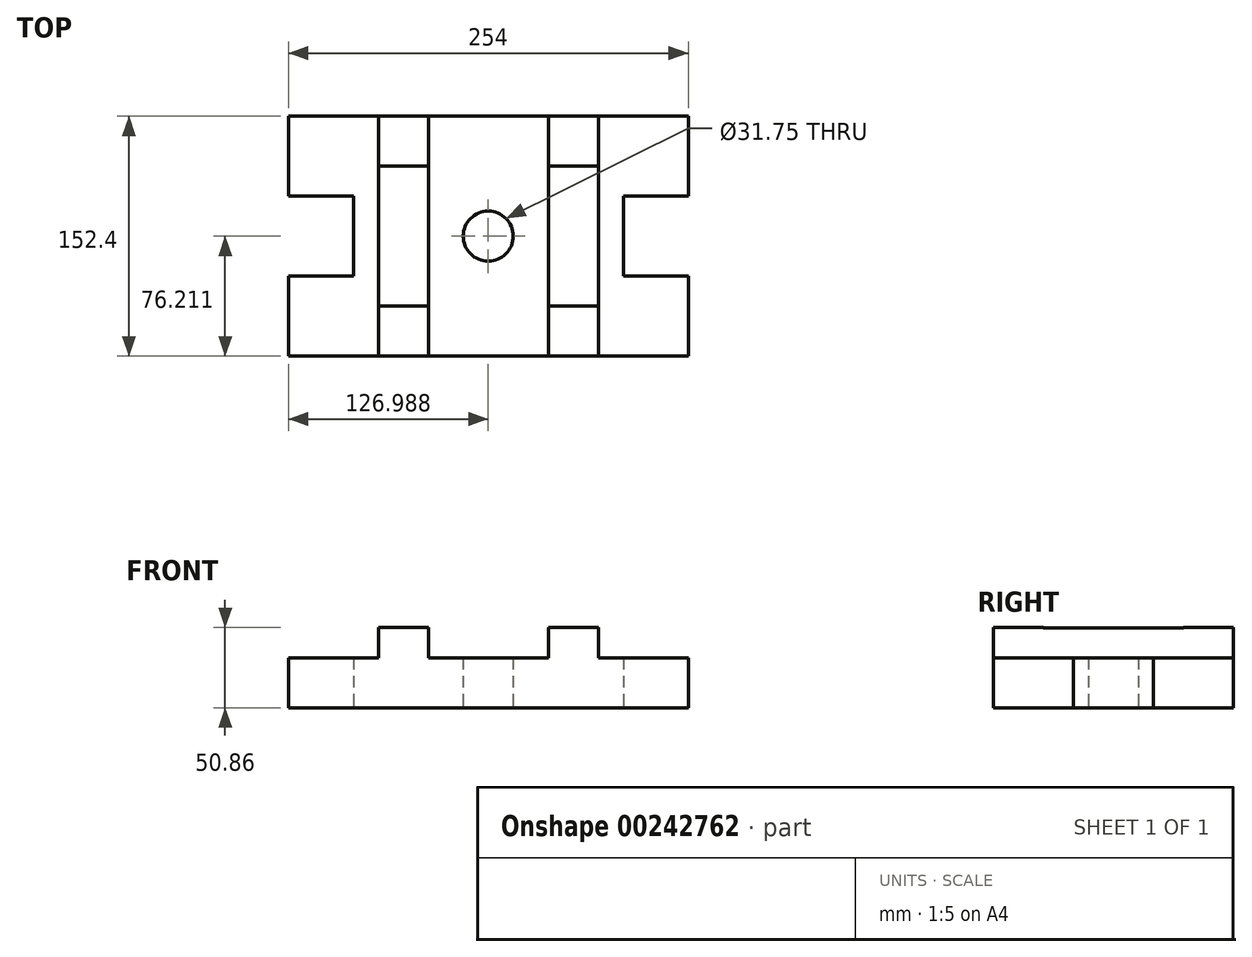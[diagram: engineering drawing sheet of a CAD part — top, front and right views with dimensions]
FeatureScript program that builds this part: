
annotation { "Feature Type Name" : "Feature", "Feature Type Description" : "" }
export const myFeature = defineFeature(function(context is Context, id is Id, definition is map)
    precondition{}
    {
        {
            var Q0;
            Q0=qCreatedBy(makeId("Top.planeOp"),FACE);
            var sketch = newSketch(context, id + "F0", { "sketchPlane" : qUnion([Q0])});
            skLineSegment(sketch, "E0.bottom", {"start": v(-75.13, 76.78) * mm, "end": v(96.32, 76.78) * mm});
            skLineSegment(sketch, "E0.top", {"start": v(-75.13, -75.62) * mm, "end": v(96.32, -75.62) * mm});
            skLineSegment(sketch, "E0.left", {"start": v(-75.13, 76.78) * mm, "end": v(-75.13, -75.62) * mm});
            skLineSegment(sketch, "E0.right", {"start": v(96.32, 76.78) * mm, "end": v(96.32, -75.62) * mm});
            skLineSegment(sketch, "E1.bottom", {"start": v(96.32, 76.78) * mm, "end": v(137.6, 76.78) * mm});
            skLineSegment(sketch, "E1.top", {"start": v(96.32, 25.98) * mm, "end": v(137.6, 25.98) * mm});
            skLineSegment(sketch, "E1.left", {"start": v(96.32, 76.78) * mm, "end": v(96.32, 25.98) * mm});
            skLineSegment(sketch, "E1.right", {"start": v(137.6, 76.78) * mm, "end": v(137.6, 25.98) * mm});
            skLineSegment(sketch, "E2.bottom", {"start": v(96.32, -75.62) * mm, "end": v(137.6, -75.62) * mm});
            skLineSegment(sketch, "E2.top", {"start": v(96.32, -24.82) * mm, "end": v(137.6, -24.82) * mm});
            skLineSegment(sketch, "E2.left", {"start": v(96.32, -75.62) * mm, "end": v(96.32, -24.82) * mm});
            skLineSegment(sketch, "E2.right", {"start": v(137.6, -75.62) * mm, "end": v(137.6, -24.82) * mm});
            skLineSegment(sketch, "E3.bottom", {"start": v(-75.13, 76.78) * mm, "end": v(-116.4, 76.78) * mm});
            skLineSegment(sketch, "E3.top", {"start": v(-75.13, 25.98) * mm, "end": v(-116.4, 25.98) * mm});
            skLineSegment(sketch, "E3.left", {"start": v(-75.13, 76.78) * mm, "end": v(-75.13, 25.98) * mm});
            skLineSegment(sketch, "E3.right", {"start": v(-116.4, 76.78) * mm, "end": v(-116.4, 25.98) * mm});
            skLineSegment(sketch, "E4.bottom", {"start": v(-75.13, -75.62) * mm, "end": v(-116.4, -75.62) * mm});
            skLineSegment(sketch, "E4.top", {"start": v(-75.13, -24.82) * mm, "end": v(-116.4, -24.82) * mm});
            skLineSegment(sketch, "E4.left", {"start": v(-75.13, -75.62) * mm, "end": v(-75.13, -24.82) * mm});
            skLineSegment(sketch, "E4.right", {"start": v(-116.4, -75.62) * mm, "end": v(-116.4, -24.82) * mm});
            skLineSegment(sketch, "E5.bottom", {"start": v(-59.26, 76.78) * mm, "end": v(80.44, 76.78) * mm});
            skLineSegment(sketch, "E5.top", {"start": v(-59.26, -75.62) * mm, "end": v(80.44, -75.62) * mm});
            skLineSegment(sketch, "E6", {"start": v(-75.13, -75.62) * mm, "end": v(-59.26, -75.62) * mm});
            skLineSegment(sketch, "E7.bottom", {"start": v(-59.26, 76.78) * mm, "end": v(-27.5, 76.78) * mm});
            skLineSegment(sketch, "E7.top", {"start": v(-59.26, -75.62) * mm, "end": v(-27.5, -75.62) * mm});
            skLineSegment(sketch, "E8.bottom", {"start": v(80.44, 76.78) * mm, "end": v(48.7, 76.78) * mm});
            skLineSegment(sketch, "E8.top", {"start": v(80.44, -75.62) * mm, "end": v(48.7, -75.62) * mm});
            skLineSegment(sketch, "E9.bottom", {"start": v(48.7, 76.78) * mm, "end": v(80.44, 76.78) * mm});
            skLineSegment(sketch, "E9.top", {"start": v(48.7, -75.62) * mm, "end": v(80.44, -75.62) * mm});
            skLineSegment(sketch, "E10", {"start": v(137.6, -75.62) * mm, "end": v(10.6, -75.62) * mm});
            skLineSegment(sketch, "E11", {"start": v(-75.13, -75.62) * mm, "end": v(-75.13, 0.58) * mm});
            skCircle(sketch, "E12", {"center": v(10.58, 0.6) * mm, "radius": 15.88 * mm});
            skSolve(sketch);
        }
        {
            var Q0;
            Q0=makeQuery(id+"F0.imprint","IMPRINT",FACE,{"disambiguationData":[TD([[makeQuery(id+"F0.imprint","IMPRINT",EDGE,{"derivedFrom":sQuery(id+"F0.wireOp",EDGE,"E3.bottom")}),1.0]])]});
            var Q1;
            Q1=makeQuery(id+"F0.imprint","IMPRINT",FACE,{"disambiguationData":[TD([[makeQuery(id+"F0.imprint","IMPRINT",EDGE,{"derivedFrom":sQuery(id+"F0.wireOp",EDGE,"E4.bottom")}),-1.0]])]});
            var Q2;
            Q2=makeQuery(id+"F0.imprint","IMPRINT",FACE,{"disambiguationData":[TD([[makeQuery(id+"F0.imprint","IMPRINT",EDGE,{"derivedFrom":sQuery(id+"F0.wireOp",EDGE,"E2.bottom")}),1.0]])]});
            var Q3;
            Q3=makeQuery(id+"F0.imprint","IMPRINT",FACE,{"disambiguationData":[TD([[makeQuery(id+"F0.imprint","IMPRINT",EDGE,{"derivedFrom":sQuery(id+"F0.wireOp",EDGE,"E1.bottom")}),-1.0]])]});
            var Q4;
            Q4=makeQuery(id+"F0.imprint","IMPRINT",FACE,{"disambiguationData":[TD([[makeQuery(id+"F0.imprint","IMPRINT",EDGE,{"derivedFrom":sQuery(id+"F0.wireOp",EDGE,"E0.bottom")}),-1.0]])]});
            var Q5;
            Q5 = qSketchRegion(id + "F2", true);
            var Q6;
            Q6=makeQuery(id+"F0.imprint","IMPRINT",FACE,{"disambiguationData":[TD([[makeQuery(id+"F0.imprint","IMPRINT",EDGE,{"derivedFrom":sQuery(id+"F0.wireOp",EDGE,"E2.top")}),-1.0]])]});
            extrude(context, id + "F1", {"entities" : qUnion([Q0, Q1, Q2, Q3, Q4, Q5, Q6]), "depth" : 31.75 * mm});
        }
        {
            var Q0;
            Q0=makeQuery(id+"F1.opExtrude","CAP_FACE",FACE,{"disambiguationData":[OSD([sQuery(id+"F0.wireOp",EDGE,"E0.bottom"),sQuery(id+"F0.wireOp",EDGE,"E0.top"),sQuery(id+"F0.wireOp",EDGE,"E0.left"),sQuery(id+"F0.wireOp",EDGE,"E0.right"),sQuery(id+"F0.wireOp",EDGE,"E1.bottom"),sQuery(id+"F0.wireOp",EDGE,"E1.top"),sQuery(id+"F0.wireOp",EDGE,"E1.right"),sQuery(id+"F0.wireOp",EDGE,"E2.bottom"),sQuery(id+"F0.wireOp",EDGE,"E2.top"),sQuery(id+"F0.wireOp",EDGE,"E2.right"),sQuery(id+"F0.wireOp",EDGE,"E3.bottom"),sQuery(id+"F0.wireOp",EDGE,"E3.top"),sQuery(id+"F0.wireOp",EDGE,"E3.right"),sQuery(id+"F0.wireOp",EDGE,"E4.bottom"),sQuery(id+"F0.wireOp",EDGE,"E4.top"),sQuery(id+"F0.wireOp",EDGE,"E4.right"),sQuery(id+"F0.wireOp",EDGE,"E5.bottom"),sQuery(id+"F0.wireOp",EDGE,"E5.top"),sQuery(id+"F0.wireOp",EDGE,"E6"),sQuery(id+"F0.wireOp",EDGE,"E7.bottom"),sQuery(id+"F0.wireOp",EDGE,"E7.top"),sQuery(id+"F0.wireOp",EDGE,"E9.bottom"),sQuery(id+"F0.wireOp",EDGE,"E9.top")])],"isStart":false});
            var sketch = newSketch(context, id + "F2", { "sketchPlane" : qUnion([Q0])});
            skLineSegment(sketch, "E13.bottom", {"start": v(-59.26, 76.78) * mm, "end": v(80.44, 76.78) * mm});
            skLineSegment(sketch, "E13.top", {"start": v(-59.26, -75.62) * mm, "end": v(80.44, -75.62) * mm});
            skLineSegment(sketch, "E13.left", {"start": v(-59.26, 76.78) * mm, "end": v(-59.26, -75.62) * mm});
            skLineSegment(sketch, "E13.right", {"start": v(80.44, 76.78) * mm, "end": v(80.44, -75.62) * mm});
            skLineSegment(sketch, "E14", {"start": v(96.32, 25.98) * mm, "end": v(96.32, 76.78) * mm});
            skLineSegment(sketch, "E15", {"start": v(96.32, 25.98) * mm, "end": v(96.32, -75.62) * mm});
            skLineSegment(sketch, "E16", {"start": v(-75.13, -75.62) * mm, "end": v(-75.13, 76.78) * mm});
            skSolve(sketch);
        }
        {
            var Q0;
            Q0=makeQuery(id+"F2.imprint","IMPRINT",FACE,{"disambiguationData":[TD([[makeQuery(id+"F2.imprint","IMPRINT",EDGE,{"derivedFrom":sQuery(id+"F2.wireOp",EDGE,"E13.bottom")}),1.0]])]});
            extrude(context, id + "F3", {"entities" : qUnion([Q0]), "operationType" : NewBodyOperationType.ADD, "depth" : 7 / 203.2 * mm});
        }
        {
            var Q0;
            Q0=makeQuery(id+"F3.opExtrude","CAP_FACE",FACE,{"disambiguationData":[OSD([sQuery(id+"F2.wireOp",EDGE,"E13.bottom"),sQuery(id+"F2.wireOp",EDGE,"E13.top"),sQuery(id+"F2.wireOp",EDGE,"E13.left"),sQuery(id+"F2.wireOp",EDGE,"E13.right")])],"isStart":false});
            var sketch = newSketch(context, id + "F4", { "sketchPlane" : qUnion([Q0])});
            skLineSegment(sketch, "E17.bottom", {"start": v(-59.26, 76.78) * mm, "end": v(-27.5, 76.78) * mm});
            skLineSegment(sketch, "E17.top", {"start": v(-59.26, -75.62) * mm, "end": v(-27.5, -75.62) * mm});
            skLineSegment(sketch, "E17.left", {"start": v(-59.26, 76.78) * mm, "end": v(-59.26, -75.62) * mm});
            skLineSegment(sketch, "E17.right", {"start": v(-27.5, 76.78) * mm, "end": v(-27.5, -75.62) * mm});
            skLineSegment(sketch, "E18.bottom", {"start": v(80.44, -75.62) * mm, "end": v(48.7, -75.62) * mm});
            skLineSegment(sketch, "E18.top", {"start": v(80.44, 76.78) * mm, "end": v(48.7, 76.78) * mm});
            skLineSegment(sketch, "E18.left", {"start": v(80.44, -75.62) * mm, "end": v(80.44, 76.78) * mm});
            skLineSegment(sketch, "E18.right", {"start": v(48.7, -75.62) * mm, "end": v(48.7, 76.78) * mm});
            skSolve(sketch);
        }
        {
            var Q0;
            Q0 = qSketchRegion(id + "F4", true);
            extrude(context, id + "F5", {"entities" : qUnion([Q0]), "operationType" : NewBodyOperationType.ADD, "depth" : 19.05 * mm});
        }
        {
            var Q0;
            Q0=makeQuery(id+"F5.opExtrude","CAP_FACE",FACE,{"disambiguationData":[OSD([sQuery(id+"F4.wireOp",EDGE,"E17.bottom"),sQuery(id+"F4.wireOp",EDGE,"E17.top"),sQuery(id+"F4.wireOp",EDGE,"E17.left"),sQuery(id+"F4.wireOp",EDGE,"E17.right")])],"isStart":false});
            var sketch = newSketch(context, id + "F6", { "sketchPlane" : qUnion([Q0])});
            skLineSegment(sketch, "E19.bottom", {"start": v(-59.26, 76.78) * mm, "end": v(-27.5, 76.78) * mm});
            skLineSegment(sketch, "E19.top", {"start": v(-59.26, 45.03) * mm, "end": v(-27.5, 45.03) * mm});
            skLineSegment(sketch, "E19.left", {"start": v(-59.26, 76.78) * mm, "end": v(-59.26, 45.03) * mm});
            skLineSegment(sketch, "E19.right", {"start": v(-27.5, 76.78) * mm, "end": v(-27.5, 45.03) * mm});
            skLineSegment(sketch, "E20.bottom", {"start": v(-27.5, -75.62) * mm, "end": v(-59.26, -75.62) * mm});
            skLineSegment(sketch, "E20.top", {"start": v(-27.5, -43.87) * mm, "end": v(-59.26, -43.87) * mm});
            skLineSegment(sketch, "E20.left", {"start": v(-27.5, -75.62) * mm, "end": v(-27.5, -43.87) * mm});
            skLineSegment(sketch, "E20.right", {"start": v(-59.26, -75.62) * mm, "end": v(-59.26, -43.87) * mm});
            skSolve(sketch);
        }
        {
            var Q0;
            Q0=makeQuery(id+"F5.opExtrude","CAP_FACE",FACE,{"disambiguationData":[OSD([sQuery(id+"F4.wireOp",EDGE,"E18.bottom"),sQuery(id+"F4.wireOp",EDGE,"E18.top"),sQuery(id+"F4.wireOp",EDGE,"E18.left"),sQuery(id+"F4.wireOp",EDGE,"E18.right")])],"isStart":false});
            var sketch = newSketch(context, id + "F7", { "sketchPlane" : qUnion([Q0])});
            skLineSegment(sketch, "E21.bottom", {"start": v(48.7, 76.78) * mm, "end": v(80.44, 76.78) * mm});
            skLineSegment(sketch, "E21.top", {"start": v(48.7, 45.03) * mm, "end": v(80.44, 45.03) * mm});
            skLineSegment(sketch, "E21.left", {"start": v(48.7, 76.78) * mm, "end": v(48.7, 45.03) * mm});
            skLineSegment(sketch, "E21.right", {"start": v(80.44, 76.78) * mm, "end": v(80.44, 45.03) * mm});
            skLineSegment(sketch, "E22.bottom", {"start": v(80.44, -75.62) * mm, "end": v(48.7, -75.62) * mm});
            skLineSegment(sketch, "E22.top", {"start": v(80.44, -43.87) * mm, "end": v(48.7, -43.87) * mm});
            skLineSegment(sketch, "E22.left", {"start": v(80.44, -75.62) * mm, "end": v(80.44, -43.87) * mm});
            skLineSegment(sketch, "E22.right", {"start": v(48.7, -75.62) * mm, "end": v(48.7, -43.87) * mm});
            skSolve(sketch);
        }
        {
            var Q0;
            Q0 = qSketchRegion(id + "F7", true);
            var Q1;
            Q1=makeQuery(id+"F6.imprint","IMPRINT",FACE,{"disambiguationData":[TD([[makeQuery(id+"F6.imprint","IMPRINT",EDGE,{"derivedFrom":sQuery(id+"F6.wireOp",EDGE,"E19.bottom")}),1.0]])]});
            var Q2;
            Q2=makeQuery(id+"F6.imprint","IMPRINT",FACE,{"disambiguationData":[TD([[makeQuery(id+"F6.imprint","IMPRINT",EDGE,{"derivedFrom":sQuery(id+"F6.wireOp",EDGE,"E20.bottom")}),-1.0]])]});
            extrude(context, id + "F8", {"entities" : qUnion([Q0, Q1, Q2]), "operationType" : NewBodyOperationType.ADD, "depth" : 3 / 101.6 * mm});
        }
    });
